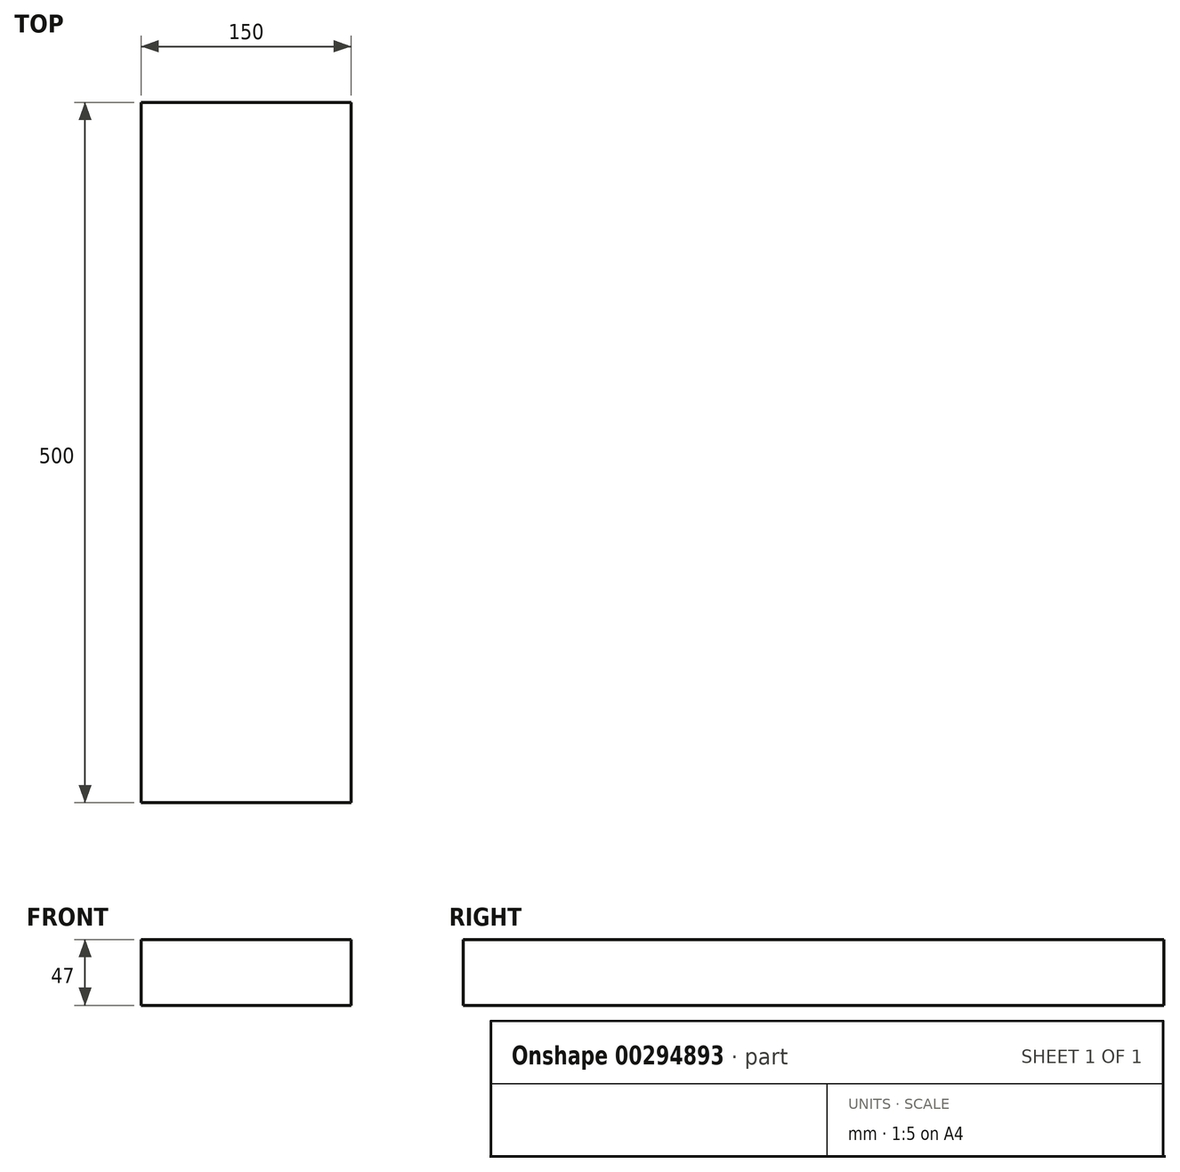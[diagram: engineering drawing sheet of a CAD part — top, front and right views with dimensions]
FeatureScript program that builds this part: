
annotation { "Feature Type Name" : "Feature", "Feature Type Description" : "" }
export const myFeature = defineFeature(function(context is Context, id is Id, definition is map)
    precondition{}
    {
        {
            var Q0;
            Q0=qCreatedBy(makeId("Front.planeOp"),FACE);
            var sketch = newSketch(context, id + "F0", { "sketchPlane" : qUnion([Q0])});
            skLineSegment(sketch, "E0.bottom", {"start": v(75, 23.5) * mm, "end": v(-75, 23.5) * mm});
            skLineSegment(sketch, "E0.top", {"start": v(75, -23.5) * mm, "end": v(-75, -23.5) * mm});
            skLineSegment(sketch, "E0.left", {"start": v(75, 23.5) * mm, "end": v(75, -23.5) * mm});
            skLineSegment(sketch, "E0.right", {"start": v(-75, 23.5) * mm, "end": v(-75, -23.5) * mm});
            skPoint(sketch, "E0.middle", {"position": v(0, 0) * mm});
            skSolve(sketch);
        }
        {
            var Q0;
            Q0 = qSketchRegion(id + "F0", true);
            extrude(context, id + "F1", {"entities" : qUnion([Q0]), "depth" : 500 * mm});
        }
    });
